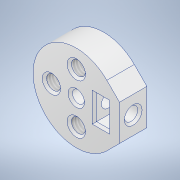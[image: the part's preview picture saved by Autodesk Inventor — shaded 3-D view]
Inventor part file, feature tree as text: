
AUTODESK INVENTOR PART (.ipt)
format: ipt  version: 2022 (Build 260153000, 153)  size: 196,096 bytes
history: native  units: mm
features: sketch x3, extrude x2, hole x2, pattern_circular x1, chamfer x1
ambient origin geometry x8: Origin, YZ Plane, XZ Plane, XY Plane, X Axis, Y Axis, Z Axis, Center Point
bodies: Solid1 (feature_tree)
feature tree (9):
  extrude  "Extrusion1"  Depth=20.0mm
  hole  "Hole1"  [1 undecoded]
  pattern_circular  "Circular Pattern1"  [2 undecoded]
  extrude  "Extrusion3"  Depth=10.0mm
  hole  "Hole3"  [1 undecoded]
  chamfer  "Chamfer1"  Angle=135.0deg  [1 undecoded]
  sketch  "Sketch2"  dims[d0=2.8mm d1=20.0mm]
  sketch  "Sketch5"  dims[d2=6.35mm d3=0.0mm]
  sketch  "Sketch6"  dims[d5=3.242mm d6=8.0mm d7=6.3mm d8=2.0mm d9=90.0deg d10=8.0mm d11=20.594885mm d12=40.0mm d13=360.0deg d28=5.8mm d29=3.0mm d30=10.0mm d31=0.0mm d33=135.0deg d34=4.25mm d35=3.1mm d36=6.0mm d37=6.3mm d38=2.0mm d39=90.0deg d40=10.0mm d41=0.0mm d42=0.5mm d43=2.0mm d44=45.0deg]
note: 5 required parameter values undecoded (feature->parameter linkage not recoverable at this tier; creation-order binding heuristic only, values carry confidence <= 0.55)
